# Revit family: PF 15
name_source: partatom
category: Lighting Fixtures
units: mm (PartAtom-declared; Revit-internal decimal feet)

## family parameters
Cut with Voids When Loaded = No
Host = Face
Light Source = Yes
OmniClass Number = 23.80.70.11
OmniClass Title = Luminaries for Internal Lighting
Part Type = Normal
Room Calculation Point = No
Round Connector Dimension = Use Diameter
Shared = No

## types (1)
- PF 15 1700lm 12W 3000K CRI85-110°
    Beam angle (°) = 110°
    Body material = White Powder Coated Aluminium
    CRI L'indice di Resa Cromatica = 85
    Codice = 3825-01-21
    Color Filter = 16777215
    Description = La plafoniera PF 15 coniuga le linee geometriche essenziali del quadrato ed un profilo estremamente sottile con fonti luminose LED COB di ultima generazione.
PF 15 può essere impiegata a soffitto o a parete, in ambienti di varia natura come ad esempio alberghi, spazi pubblici o privati, anche con altezze ridotte. Costituisce un'alternativa ai punti luce ad incasso, con notevoli economie di installazione. Lo schermo di chiusura è in policarbonato opale ad alta capacità diffondente, e sporge leggermente rispetto al profilo del prodotto, con un effetto luminoso inedito.
    Dimming Lamp Color Temperature Shift = <None>
    Effective Intensity (lm) = 1088
    Glass material = Glass
    Lamp = LED 1700lm 12W 3000K CRI85
    Larghezza = 150 mm
    Manufacturer = ARIA
    Model = 3825-01-21
    Photometric Web File = 3825-01 _ PF 15 LED 12W 1700 lm.IES
    Tilt Angle = 90.00°
    Type Comments = Ceiling / Wall light
    Type Image = PF15_TAB-Sito-Ivela_ok.jpg
    URL = https://www.aria.lighting
    Wattage Comments = 12

## geometry (parser evidence)
native form markers: Sweep x3
no freeform markers — native parametric forms only
